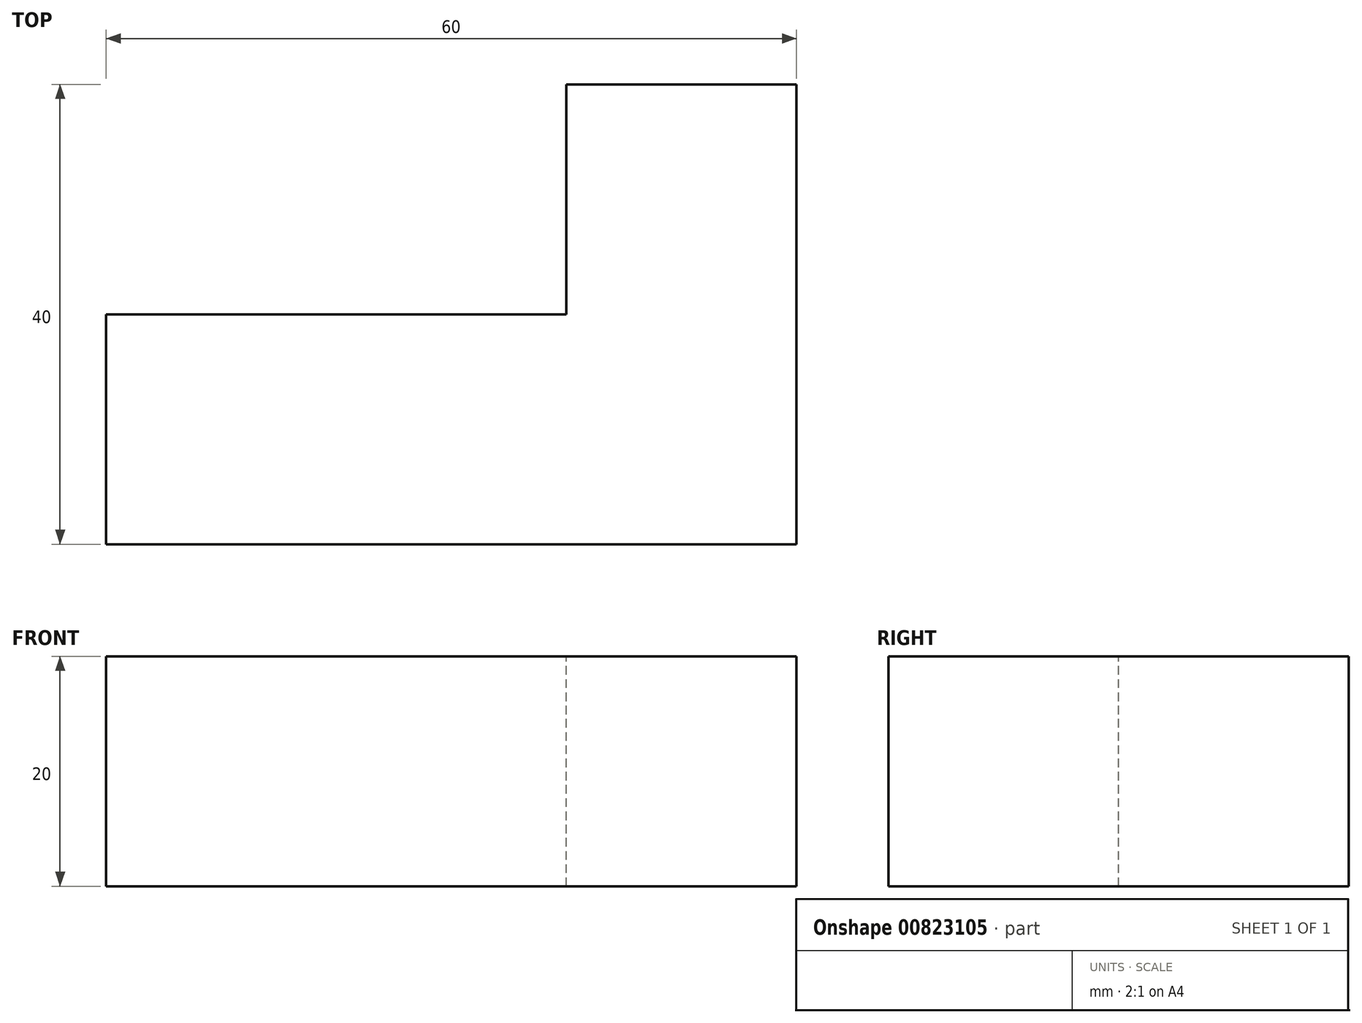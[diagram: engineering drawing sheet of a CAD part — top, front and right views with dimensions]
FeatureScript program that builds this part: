
annotation { "Feature Type Name" : "Feature", "Feature Type Description" : "" }
export const myFeature = defineFeature(function(context is Context, id is Id, definition is map)
    precondition{}
    {
        {
            var Q0;
            Q0=qCreatedBy(makeId("Front.planeOp"),FACE);
            var sketch = newSketch(context, id + "F0", { "sketchPlane" : qUnion([Q0])});
            skLineSegment(sketch, "E0.bottom", {"start": v(10, 10) * mm, "end": v(-10, 10) * mm});
            skLineSegment(sketch, "E0.top", {"start": v(10, -10) * mm, "end": v(-10, -10) * mm});
            skLineSegment(sketch, "E0.left", {"start": v(10, 10) * mm, "end": v(10, -10) * mm});
            skLineSegment(sketch, "E0.right", {"start": v(-10, 10) * mm, "end": v(-10, -10) * mm});
            skPoint(sketch, "E0.middle", {"position": v(0, 0) * mm});
            skSolve(sketch);
        }
        {
            var Q0;
            Q0=makeQuery(id+"F0.imprint","IMPRINT",FACE,{"disambiguationData":[TD([[makeQuery(id+"F0.imprint","IMPRINT",EDGE,{"derivedFrom":sQuery(id+"F0.wireOp",EDGE,"E0.bottom")}),1.0]])]});
            extrude(context, id + "F1", {"entities" : qUnion([Q0]), "depth" : 40 * mm, "offsetDistance" : 25.4 * mm});
        }
        {
            var Q0;
            Q0=makeQuery(id+"F1.opExtrude","SWEPT_FACE",FACE,{"disambiguationData":[OSD([sQuery(id+"F0.wireOp",EDGE,"E0.right")])]});
            var sketch = newSketch(context, id + "F2", { "sketchPlane" : qUnion([Q0])});
            skLineSegment(sketch, "E1.bottom", {"start": v(40, -10) * mm, "end": v(20, -10) * mm});
            skLineSegment(sketch, "E1.top", {"start": v(40, 10) * mm, "end": v(20, 10) * mm});
            skLineSegment(sketch, "E1.left", {"start": v(40, -10) * mm, "end": v(40, 10) * mm});
            skLineSegment(sketch, "E1.right", {"start": v(20, -10) * mm, "end": v(20, 10) * mm});
            skSolve(sketch);
        }
        {
            var Q0;
            Q0 = qSketchRegion(id + "F2", true);
            extrude(context, id + "F3", {"entities" : qUnion([Q0]), "operationType" : NewBodyOperationType.ADD, "depth" : 40 * mm, "offsetDistance" : 25.4 * mm});
        }
    });
